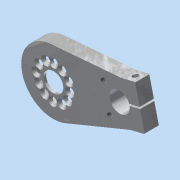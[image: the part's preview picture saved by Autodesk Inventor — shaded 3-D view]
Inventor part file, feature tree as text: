
AUTODESK INVENTOR PART (.ipt)
format: ipt  version: 2015 SP1 (Build 190203100, 203)  size: 1,571,840 bytes
history: native  units: in
note: dims shown in document units (in); Inventor stores cm internally (conversion verified against a paired STEP export)
features: sketch x8, projected_geometry x7, extrude x6, fillet x3, chamfer x2, other x1, hole x1, plane x1, thread x1, mirror x1
ambient origin geometry x8: Origin, YZ Plane, XZ Plane, XY Plane, X Axis, Y Axis, Z Axis, Center Point
bodies: Solid1 (feature_tree)
feature tree (31):
  other  "mount_sketch_alt.ipt"
  extrude  "Extrusion1"  Depth=0.5in TaperAngle=0.0deg
  extrude  "Extrusion2"  Depth=1.9882in
  hole  "Hole1"  [1 undecoded]
  sketch  "Sketch4"  dims[d6=0.4062in d7=0.0in]
  extrude  "Extrusion3"  Depth=0.5in
  plane  "Work Plane1"
  chamfer  "Chamfer2"  Distance=0.375in
  extrude  "Extrusion6"  Depth=0.5in
  fillet  "Fillet6"  Radius=0.25in
  fillet  "Fillet7"  Radius=0.5in
  extrude  "Extrusion10"  Depth=0.03in
  fillet  "Fillet10"  Radius=0.0125in
  extrude  "Extrusion11"  Depth=0.03in
  thread  "Thread2"  [1 undecoded]
  mirror  "Mirror2"
  sketch  "Sketch19"  dims[d81=0.25in d82=0.0in d84=0.03in d88=0.0125in d89=0.125in d90=45.0deg d91=0.3in d92=0.3in d93=0.9843in d94=0.19in d95=0.35in d97=1.0in d98=0.0in d99=1.0in d100=0.0in d101=1.2in d102=2.3797in d103=2.4104in d104=2.4029in d105=4.282in]
  chamfer  "Chamfer3"  Distance=0.9843in
  sketch  "Sketch18"  dims[d49=0.0787in d50=0.125in d51=45.0deg d55=0.4in d58=0.25in d59=0.0in d61=0.4in d70=0.5in]
  sketch  "Sketch2"  dims[d0=0.3937in d1=0.5in d2=0.0in]
  sketch  "Sketch3"  dims[d4=0.0272in d5=1.9882in]
  projected_geometry  "Projected Loop1"
  projected_geometry  "Projected Loop2"
  sketch  "Sketch8"  dims[d8=0.1693in d9=0.75in d10=0.375in d11=0.25in d12=0.5635in d13=1.0in d14=0.8108in d15=0.201in]
  projected_geometry  "Projected Loop7"
  sketch  "Sketch13"  dims[d17=0.2375in d18=0.5in]
  projected_geometry  "Projected Loop11"
  sketch  "Sketch17"  dims[d19=0.25in d20=0.375in d21=0.0in]
  projected_geometry  "Projected Loop17"
  projected_geometry  "Projected Loop18"
  projected_geometry  "Projected Loop19"
note: 2 required parameter values undecoded (feature->parameter linkage not recoverable at this tier; creation-order binding heuristic only, values carry confidence <= 0.55)
